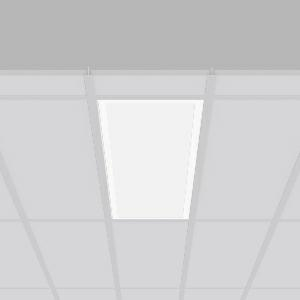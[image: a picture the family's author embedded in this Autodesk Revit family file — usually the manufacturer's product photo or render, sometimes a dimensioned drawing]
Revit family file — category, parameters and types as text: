
# Revit family: sidelite_eco_672376_002_1bf0
name_source: partatom
category: Lighting Fixtures
units: mm (PartAtom-declared; Revit-internal decimal feet)

## family parameters
Cut with Voids When Loaded = No
Host = Face
Light Source = No
Part Type = Normal
Room Calculation Point = No
Round Connector Dimension = Use Diameter
Shared = No

## types (1)
- SIDELITE ECO (1 x LED Modul 830, 3300 lm, 3000)
    Apparent Load = 29 VA
    CIE Flux Codes = 47 79 96 100 100
    Color Rendering = 80
    Color Temperature = 3000
    Default Elevation = 1800 mm
    Description = Series: SIDELITE ECO
Highly economical recessed luminaire with progressive LED technology. For escape route illumination. Frame made of aluminium, powder-coated. Diffuser: plastic, opal. Lightguide and diffuser made of non-yellowing plastic (PMMA). Lateral light emission (RZB SIDELITE technology) for homogeneous light distribution. External driver. Second cable inlet for loop through. External driver with simple plug-in locking system. Extended connection cable (1.90 m). Suitable for connection to central battery systems. 
Colour: white
Length: 1245 mm
Width: 308 mm
Cut-out length: 1220 mm
Cut-out width: 285 mm
Recess height: 160 mm
Luminaire: recess height: 40 mm
Weight: 3.64 kg
Operating mode: maintained power mode
Lamp: LED
Socket: without socket
Colour temperature: 3000K
Colour rendering index (CRI): 80
System power: 29 W
Rated luminous flux: 3300 lm
Luminous flux, emergency: 3300 lm
System power, emergency: 29 W
Control gear: Regulated power supply
Protection class: II
Type of protection: IP 20
    Height = 0 mm  [stored 0 ft]
    Lamp = 1 x LED Modul 830
    Lamp Light Flux = 3300 lm
    Lamp count = 1
    Length = 1245 mm
    Lifetime = 50000 h
    Luminous efficacy = 114 lm/W
    Manufacturer = RZB
    ModVariant = No
    Model = 672376.002
    Mounting Place = Ceiling
    Mounting Type = Recessed
    Number of Poles = 1
    OnlyDefault = Yes
    Power Factor = 1
    Product Name = SIDELITE ECO
    Product group = Recessed modular luminaires
    ProductGroupID = 406
    Protection Class = Protection class II
    Protection Degree = IP 20
    RLX_Detail_Level = 1
    RLX_Emergency_Light_Flux = 3300 lm
    RLX_Emergency_Type = 3
    RLX_Emergency_Type_DB = Yes
    RlxData = <blob elided: 30069 chars, md5=53ef0a70>
    Socket = socket
    Standby Power = 0 W
    System Light Flux = 3300 lm
    System Power = 29 W
    Type Comments = Product without accessories
    Type Image = 312367.002.jpg
    URL = http://relux.com
    VarID = ---
    Voltage = 230 V
    Voltage Range = 220-240 V
    Weight = 0.00 kg
    Width = 308 mm

note: [stored X ft] marks values corroborated as IEEE doubles in the binary element streams (Revit-internal decimal feet)

## geometry (parser evidence)
native form markers: Blend x4, Sweep x11
no freeform markers — native parametric forms only
